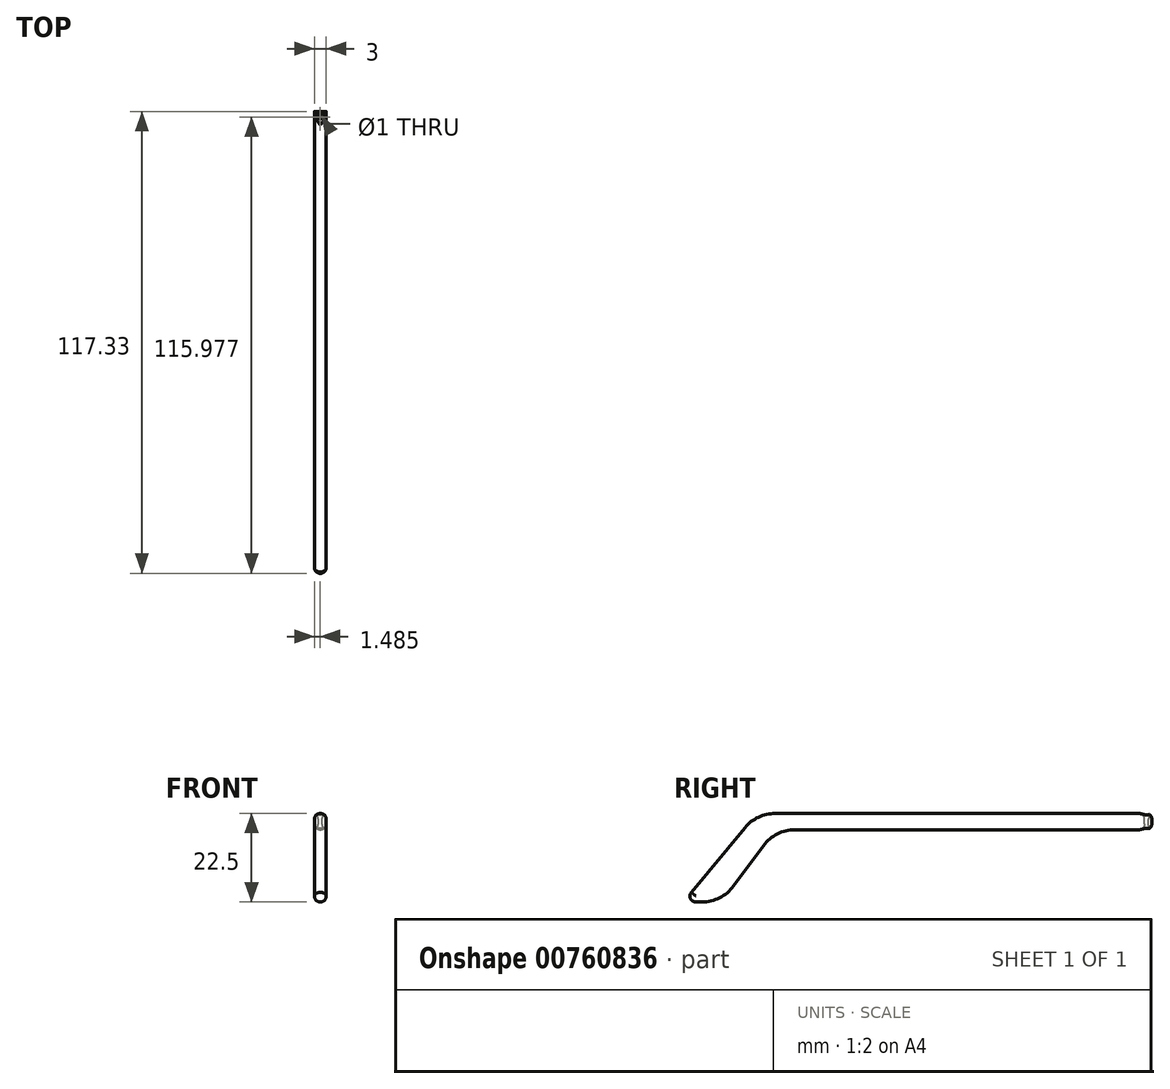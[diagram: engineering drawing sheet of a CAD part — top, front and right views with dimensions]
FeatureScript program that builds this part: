
annotation { "Feature Type Name" : "Feature", "Feature Type Description" : "" }
export const myFeature = defineFeature(function(context is Context, id is Id, definition is map)
    precondition{}
    {
        {
            var Q0;
            Q0=qCreatedBy(makeId("Right.planeOp"),FACE);
            var sketch = newSketch(context, id + "F0", { "sketchPlane" : qUnion([Q0])});
            skLineSegment(sketch, "E0", {"start": v(58.47, 31.23) * mm, "end": v(-37.2, 31.23) * mm});
            skLineSegment(sketch, "E1", {"start": v(-44.9, 27.62) * mm, "end": v(-60.54, 8.73) * mm});
            skPoint(sketch, "E2.visualSharp", {"position": v(-41.9, 31.23) * mm});
            skArc(sketch, "E2.filletArc", {"start": v(-37.2, 31.23) * mm, "mid": v(-41.45, 30.28) * mm, "end": v(-44.9, 27.62) * mm});
            skLineSegment(sketch, "E3", {"start": v(-60.54, 8.73) * mm, "end": v(-55.81, 8.73) * mm});
            skLineSegment(sketch, "E4", {"start": v(58.47, 31.23) * mm, "end": v(58.47, 27.09) * mm});
            skLineSegment(sketch, "E5", {"start": v(58.47, 27.09) * mm, "end": v(-32.15, 27.09) * mm});
            skLineSegment(sketch, "E6", {"start": v(-40.2, 23.04) * mm, "end": v(-47.77, 12.79) * mm});
            skPoint(sketch, "E7.visualSharp", {"position": v(-50.77, 8.73) * mm});
            skArc(sketch, "E7.filletArc", {"start": v(-55.81, 8.73) * mm, "mid": v(-51.31, 9.8) * mm, "end": v(-47.77, 12.79) * mm});
            skPoint(sketch, "E8.visualSharp", {"position": v(-37.2, 27.09) * mm});
            skArc(sketch, "E8.filletArc", {"start": v(-32.15, 27.09) * mm, "mid": v(-36.65, 26.02) * mm, "end": v(-40.2, 23.04) * mm});
            skSolve(sketch);
        }
        {
            var Q0;
            Q0=makeQuery(id+"F0.imprint","IMPRINT",FACE,{"disambiguationData":[TD([[makeQuery(id+"F0.imprint","IMPRINT",EDGE,{"derivedFrom":sQuery(id+"F0.wireOp",EDGE,"E0")}),1.0]])]});
            extrude(context, id + "F1", {"entities" : qUnion([Q0]), "depth" : 3 * mm, "offsetDistance" : 25 * mm});
        }
        {
            var Q0;
            Q0=makeQuery(id+"F1.opExtrude","SWEPT_FACE",FACE,{"disambiguationData":[OSD([sQuery(id+"F0.wireOp",EDGE,"E0")])]});
            var sketch = newSketch(context, id + "F2", { "sketchPlane" : qUnion([Q0])});
            skCircle(sketch, "E9", {"center": v(1.49, 57.12) * mm, "radius": 0.5 * mm});
            skSolve(sketch);
        }
        {
            var Q0;
            Q0 = qSketchRegion(id + "F2", true);
            extrude(context, id + "F3", {"entities" : qUnion([Q0]), "operationType" : NewBodyOperationType.REMOVE, "oppositeDirection" : true, "depth" : 30 * mm, "offsetDistance" : 25 * mm});
        }
        {
            var Q0;
            Q0=makeQuery(id+"F1.opExtrude","SWEPT_FACE",FACE,{"disambiguationData":[OSD([sQuery(id+"F0.wireOp",EDGE,"E0")])]});
            fillet(context, id + "F4", {"entities" : qUnion([Q0]), "radius" : 1.49 * mm, "tangentPropagation" : true, "allowEdgeOverflow" : false});
        }
        {
            var Q0;
            Q0=makeQuery(id+"F1.opExtrude","SWEPT_FACE",FACE,{"disambiguationData":[OSD([sQuery(id+"F0.wireOp",EDGE,"E5")])]});
            fillet(context, id + "F5", {"entities" : qUnion([Q0]), "radius" : 1.49 * mm, "tangentPropagation" : true, "allowEdgeOverflow" : false});
        }
    });
